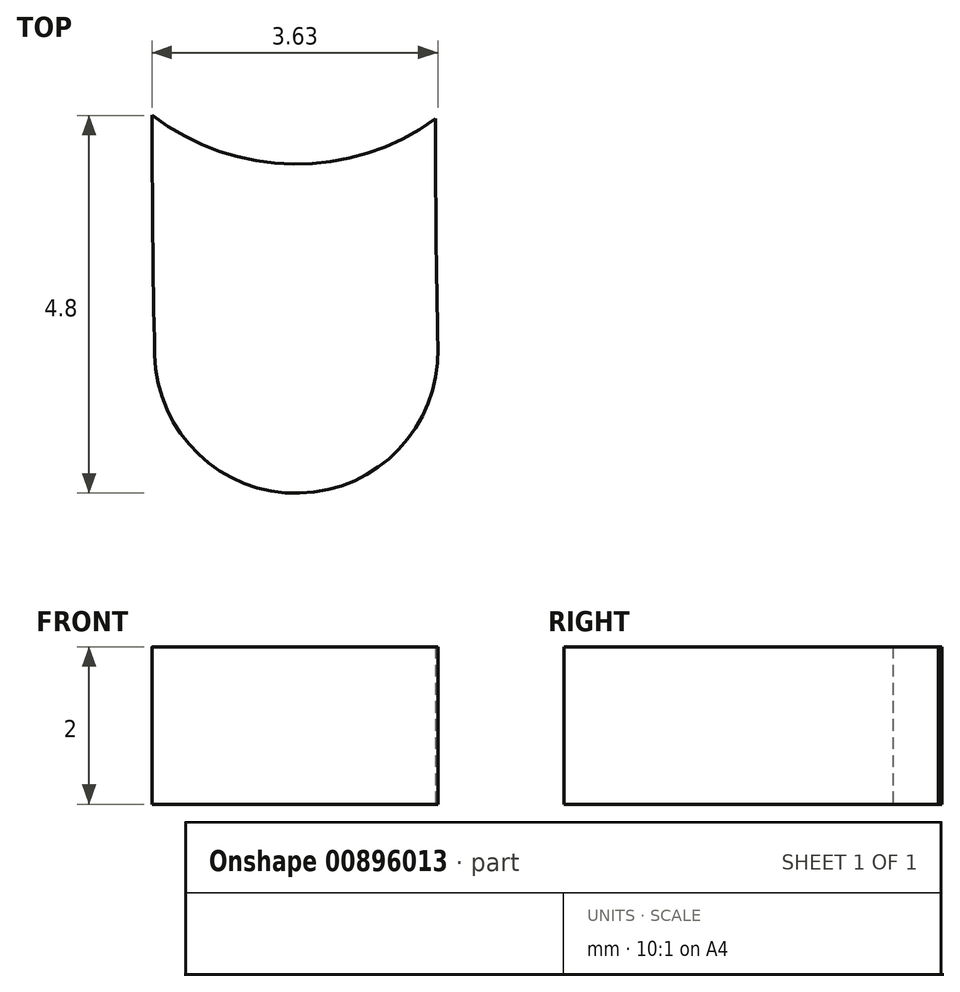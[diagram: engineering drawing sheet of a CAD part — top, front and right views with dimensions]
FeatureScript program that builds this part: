
annotation { "Feature Type Name" : "Feature", "Feature Type Description" : "" }
export const myFeature = defineFeature(function(context is Context, id is Id, definition is map)
    precondition{}
    {
        {
            var Q0;
            Q0=qCreatedBy(makeId("Top.planeOp"),FACE);
            var sketch = newSketch(context, id + "F0", { "sketchPlane" : qUnion([Q0])});
            skCircle(sketch, "E0.cCircle", {"center": v(0, 0) * mm, "radius": 22.29 * mm, "construction": true});
            skLineSegment(sketch, "E0.0", {"start": v(0, 44.57) * mm, "end": v(38.6, -22.29) * mm});
            skLineSegment(sketch, "E0.1", {"start": v(38.6, -22.29) * mm, "end": v(-38.6, -22.29) * mm});
            skLineSegment(sketch, "E0.2", {"start": v(-38.6, -22.29) * mm, "end": v(0, 44.57) * mm});
            skPoint(sketch, "E0.0.midPoint", {"position": v(19.3, 11.14) * mm});
            skLineSegment(sketch, "E1.0", {"start": v(0, 41.77) * mm, "end": v(36.18, -20.89) * mm});
            skLineSegment(sketch, "E1.1", {"start": v(-36.18, -20.89) * mm, "end": v(0, 41.77) * mm});
            skLineSegment(sketch, "E1.2", {"start": v(36.18, -20.89) * mm, "end": v(-36.18, -20.89) * mm});
            skLineSegment(sketch, "E2", {"start": v(-103.4, -22.29) * mm, "end": v(-180.6, -22.29) * mm});
            skLineSegment(sketch, "E3", {"start": v(-180.6, -22.29) * mm, "end": v(-142, 34.06) * mm});
            skLineSegment(sketch, "E4", {"start": v(-142, 34.06) * mm, "end": v(-103.4, -22.29) * mm});
            skLineSegment(sketch, "E5.0", {"start": v(-177.94, -20.89) * mm, "end": v(-142, 31.58) * mm});
            skLineSegment(sketch, "E5.1", {"start": v(-106.06, -20.89) * mm, "end": v(-177.94, -20.89) * mm});
            skLineSegment(sketch, "E5.2", {"start": v(-142, 31.58) * mm, "end": v(-106.06, -20.89) * mm});
            skSolve(sketch);
        }
        {
            var Q0;
            Q0=qCreatedBy(makeId("Top.planeOp"),FACE);
            var sketch = newSketch(context, id + "F1", { "sketchPlane" : qUnion([Q0])});
            skCircle(sketch, "E6.cCircle", {"center": v(209.04, 0) * mm, "radius": 118.8 * mm, "construction": true});
            skLineSegment(sketch, "E6.0", {"start": v(170.44, 118.8) * mm, "end": v(247.64, 118.8) * mm});
            skLineSegment(sketch, "E6.1", {"start": v(247.64, 118.8) * mm, "end": v(310.1, 73.42) * mm});
            skLineSegment(sketch, "E6.2", {"start": v(310.1, 73.42) * mm, "end": v(333.95, 0) * mm});
            skLineSegment(sketch, "E6.3", {"start": v(333.95, 0) * mm, "end": v(310.1, -73.42) * mm});
            skLineSegment(sketch, "E6.4", {"start": v(310.1, -73.42) * mm, "end": v(247.64, -118.8) * mm});
            skLineSegment(sketch, "E6.5", {"start": v(247.64, -118.8) * mm, "end": v(170.44, -118.8) * mm});
            skLineSegment(sketch, "E6.6", {"start": v(170.44, -118.8) * mm, "end": v(107.98, -73.42) * mm});
            skLineSegment(sketch, "E6.7", {"start": v(107.98, -73.42) * mm, "end": v(84.13, 0) * mm});
            skLineSegment(sketch, "E6.8", {"start": v(84.13, 0) * mm, "end": v(107.98, 73.42) * mm});
            skLineSegment(sketch, "E6.9", {"start": v(107.98, 73.42) * mm, "end": v(170.44, 118.8) * mm});
            skPoint(sketch, "E6.0.midPoint", {"position": v(209.04, 118.8) * mm});
            skLineSegment(sketch, "E7.0", {"start": v(38.6, -22.29) * mm, "end": v(-38.6, -22.29) * mm});
            skPoint(sketch, "E8.0", {"position": v(-142, -22.29) * mm});
            skLineSegment(sketch, "E9.0", {"start": v(-103.4, -22.29) * mm, "end": v(-180.6, -22.29) * mm});
            skArc(sketch, "E10", {"start": v(90.27, 2.69) * mm, "mid": v(90.24, 0) * mm, "end": v(90.27, -2.69) * mm});
            skLineSegment(sketch, "E11", {"start": v(84.13, 0) * mm, "end": v(209.04, 0) * mm, "construction": true});
            skCircle(sketch, "E12", {"center": v(90.27, 2.69) * mm, "radius": 3 * mm});
            skArc(sketch, "E13.0.startCap", {"start": v(88.47, 2.73) * mm, "mid": v(90.31, 4.49) * mm, "end": v(92.07, 2.65) * mm});
            skArc(sketch, "E13.0.endCap", {"start": v(92.07, -2.65) * mm, "mid": v(90.31, -4.49) * mm, "end": v(88.47, -2.73) * mm});
            skArc(sketch, "E13.0.left", {"start": v(92.07, 2.65) * mm, "mid": v(92.04, 0) * mm, "end": v(92.07, -2.65) * mm});
            skArc(sketch, "E13.0.right", {"start": v(88.47, 2.73) * mm, "mid": v(88.44, 0) * mm, "end": v(88.47, -2.73) * mm});
            skPoint(sketch, "E14.startSnap0", {"position": v(90.24, 0) * mm});
            skArc(sketch, "E15", {"start": v(89.8, 17.47) * mm, "mid": v(95.93, 0) * mm, "end": v(89.8, -17.47) * mm});
            skPoint(sketch, "E16.1.0", {"position": v(172.33, -112.98) * mm});
            skCircle(sketch, "E16.1.1", {"center": v(169.78, -112.12) * mm, "radius": 3 * mm});
            skArc(sketch, "E16.1.2", {"start": v(155.58, -108) * mm, "mid": v(174.09, -107.58) * mm, "end": v(188.81, -118.8) * mm});
            skArc(sketch, "E16.1.3", {"start": v(169.78, -112.12) * mm, "mid": v(172.33, -112.98) * mm, "end": v(174.9, -113.79) * mm});
            skArc(sketch, "E16.1.4", {"start": v(169.19, -113.82) * mm, "mid": v(171.77, -114.7) * mm, "end": v(174.38, -115.51) * mm});
            skArc(sketch, "E16.1.5", {"start": v(175.41, -112.06) * mm, "mid": v(176.62, -114.3) * mm, "end": v(174.38, -115.51) * mm});
            skArc(sketch, "E16.1.6", {"start": v(170.38, -110.43) * mm, "mid": v(172.89, -111.27) * mm, "end": v(175.41, -112.06) * mm});
            skArc(sketch, "E16.1.7", {"start": v(169.19, -113.82) * mm, "mid": v(168.08, -111.53) * mm, "end": v(170.38, -110.43) * mm});
            skPoint(sketch, "E16.2.0", {"position": v(305.15, -69.83) * mm});
            skCircle(sketch, "E16.2.1", {"center": v(303.54, -71.99) * mm, "radius": 3 * mm});
            skArc(sketch, "E16.2.2", {"start": v(295.23, -84.22) * mm, "mid": v(300.55, -66.49) * mm, "end": v(315.77, -55.95) * mm});
            skArc(sketch, "E16.2.3", {"start": v(303.54, -71.99) * mm, "mid": v(305.15, -69.83) * mm, "end": v(306.7, -67.63) * mm});
            skArc(sketch, "E16.2.4", {"start": v(304.98, -73.08) * mm, "mid": v(306.6, -70.89) * mm, "end": v(308.19, -68.66) * mm});
            skArc(sketch, "E16.2.5", {"start": v(305.23, -66.6) * mm, "mid": v(307.73, -66.15) * mm, "end": v(308.19, -68.66) * mm});
            skArc(sketch, "E16.2.6", {"start": v(302.11, -70.9) * mm, "mid": v(303.7, -68.77) * mm, "end": v(305.23, -66.6) * mm});
            skArc(sketch, "E16.2.7", {"start": v(304.98, -73.08) * mm, "mid": v(302.45, -73.42) * mm, "end": v(302.11, -70.9) * mm});
            skPoint(sketch, "E16.3.0", {"position": v(305.15, 69.83) * mm});
            skCircle(sketch, "E16.3.1", {"center": v(306.7, 67.63) * mm, "radius": 3 * mm});
            skArc(sketch, "E16.3.2", {"start": v(315.77, 55.95) * mm, "mid": v(300.55, 66.49) * mm, "end": v(295.23, 84.22) * mm});
            skArc(sketch, "E16.3.3", {"start": v(306.7, 67.63) * mm, "mid": v(305.15, 69.83) * mm, "end": v(303.54, 71.99) * mm});
            skArc(sketch, "E16.3.4", {"start": v(308.19, 68.66) * mm, "mid": v(306.6, 70.89) * mm, "end": v(304.98, 73.08) * mm});
            skArc(sketch, "E16.3.5", {"start": v(302.11, 70.9) * mm, "mid": v(302.45, 73.42) * mm, "end": v(304.98, 73.08) * mm});
            skArc(sketch, "E16.3.6", {"start": v(305.23, 66.6) * mm, "mid": v(303.7, 68.77) * mm, "end": v(302.11, 70.9) * mm});
            skArc(sketch, "E16.3.7", {"start": v(308.19, 68.66) * mm, "mid": v(307.73, 66.15) * mm, "end": v(305.23, 66.6) * mm});
            skPoint(sketch, "E16.4.0", {"position": v(172.33, 112.98) * mm});
            skCircle(sketch, "E16.4.1", {"center": v(174.9, 113.79) * mm, "radius": 3 * mm, "construction": true});
            skArc(sketch, "E16.4.2", {"start": v(188.81, 118.8) * mm, "mid": v(174.09, 107.58) * mm, "end": v(155.58, 108) * mm});
            skArc(sketch, "E16.4.3", {"start": v(174.9, 113.79) * mm, "mid": v(172.33, 112.98) * mm, "end": v(169.78, 112.12) * mm});
            skArc(sketch, "E16.4.4", {"start": v(174.38, 115.51) * mm, "mid": v(171.77, 114.7) * mm, "end": v(169.19, 113.82) * mm, "construction": true});
            skArc(sketch, "E16.4.5", {"start": v(170.38, 110.43) * mm, "mid": v(168.08, 111.53) * mm, "end": v(169.19, 113.82) * mm, "construction": true});
            skArc(sketch, "E16.4.6", {"start": v(175.41, 112.06) * mm, "mid": v(172.89, 111.27) * mm, "end": v(170.38, 110.43) * mm, "construction": true});
            skArc(sketch, "E16.4.7", {"start": v(174.38, 115.51) * mm, "mid": v(176.62, 114.3) * mm, "end": v(175.41, 112.06) * mm, "construction": true});
            skSolve(sketch);
        }
        {
            var Q0;
            {var subQ0=sQuery(id+"F1.wireOp",EDGE,"E13.0.endCap");Q0=makeQuery(id+"F1.imprint","IMPRINT",FACE,{"disambiguationData":[TD([[makeQuery(id+"F1.imprint","IMPRINT",EDGE,{"derivedFrom":subQ0}),1.0]])]});}
            extrude(context, id + "F2", {"entities" : qUnion([Q0]), "depth" : 2 * mm, "offsetDistance" : 25 * mm});
        }
    });
